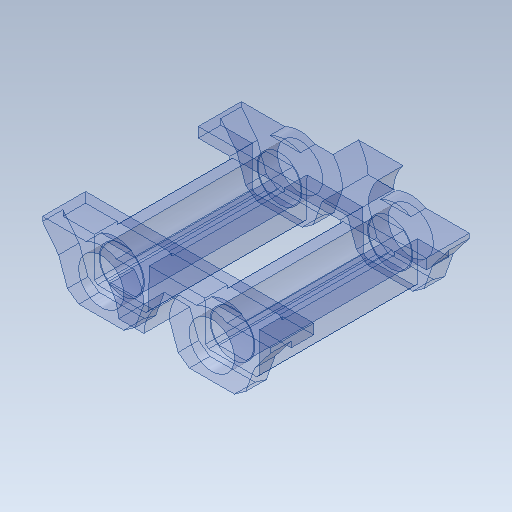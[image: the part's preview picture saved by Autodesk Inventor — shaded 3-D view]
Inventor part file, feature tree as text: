
AUTODESK INVENTOR PART (.ipt)
format: ipt  version: 2020 (Build 240168000, 168)  size: 408,576 bytes
history: native  units: mm
features: mirror x10, extrude x9, sketch x9, chamfer x2, other x1
ambient origin geometry x8: Origin, YZ Plane, XZ Plane, XY Plane, X Axis, Y Axis, Z Axis, Center Point
bodies: Body1 (feature_tree)
feature tree (31):
  other  "Bryła1"
  extrude  "Wyciągnięcie proste1"  Depth=20.0mm
  extrude  "Wyciągnięcie proste2"  Depth=20.0mm
  mirror  "Odbij1"
  extrude  "Wyciągnięcie proste3"  Depth=40.5mm
  mirror  "Odbij2"
  extrude  "Wyciągnięcie proste4"  TaperAngle=0.0deg  [1 undecoded]
  extrude  "Wyciągnięcie proste5"  Depth=40.5mm
  mirror  "Odbij3"
  mirror  "Odbij4"
  extrude  "Wyciągnięcie proste6"  TaperAngle=0.0deg  [1 undecoded]
  mirror  "Odbij5"
  mirror  "Odbij6"
  extrude  "Wyciągnięcie proste7"  Depth=56.02mm
  mirror  "Odbij7"
  chamfer  "Faza1"  Distance=28.01mm
  extrude  "Wyciągnięcie proste8"  Depth=3.6mm TaperAngle=0.0deg
  chamfer  "Faza2"  Distance=7.29mm
  mirror  "Odbij8"
  mirror  "Odbij9"
  extrude  "Wyciągnięcie proste9"  Depth=1.575mm
  mirror  "Odbij10"
  sketch  "Szkic1"
  sketch  "Szkic2"
  sketch  "Szkic3"
  sketch  "Szkic4"
  sketch  "Szkic5"
  sketch  "Szkic6"
  sketch  "Szkic7"
  sketch  "Szkic8"
  sketch  "Szkic10"
note: 2 required parameter values undecoded (feature->parameter linkage not recoverable at this tier; creation-order binding heuristic only, values carry confidence <= 0.55)
